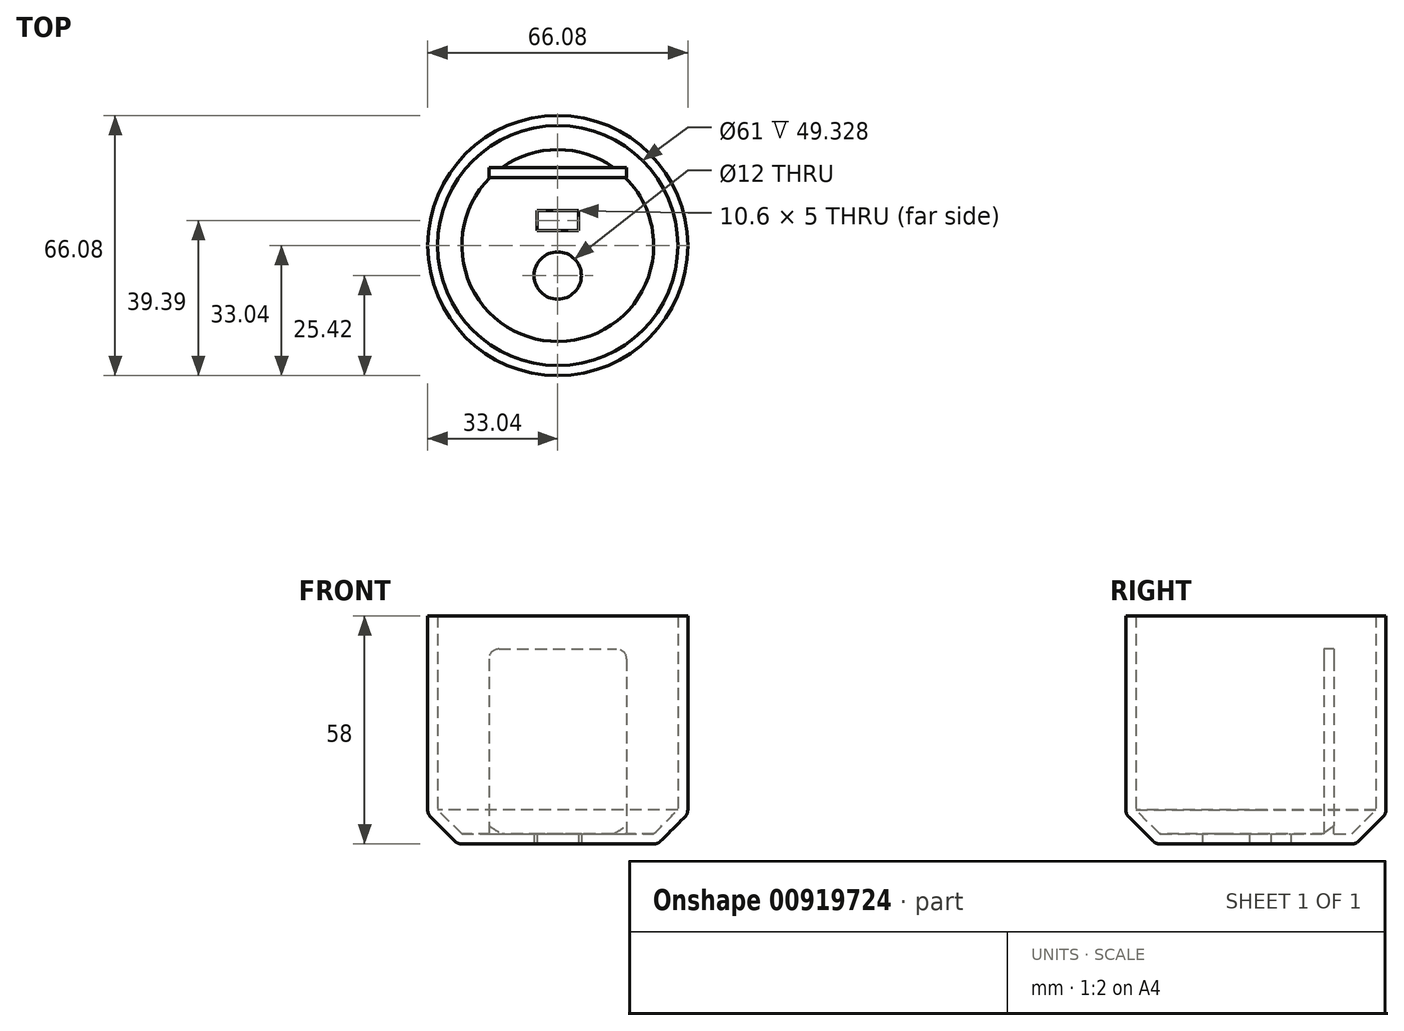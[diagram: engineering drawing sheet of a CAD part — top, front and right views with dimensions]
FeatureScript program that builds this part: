
annotation { "Feature Type Name" : "Feature", "Feature Type Description" : "" }
export const myFeature = defineFeature(function(context is Context, id is Id, definition is map)
    precondition{}
    {
        {
            var Q0;
            Q0=qCreatedBy(makeId("Top.planeOp"),FACE);
            var sketch = newSketch(context, id + "F0", { "sketchPlane" : qUnion([Q0])});
            skCircle(sketch, "E0", {"center": v(0, 0) * mm, "radius": 33.04 * mm});
            skSolve(sketch);
        }
        {
            var Q0;
            Q0 = qSketchRegion(id + "F0", true);
            extrude(context, id + "F1", {"entities" : qUnion([Q0]), "depth" : 58 * mm, "offsetDistance" : 25.4 * mm});
        }
        {
            var Q0;
            Q0=makeQuery(id+"F1.opExtrude","CAP_EDGE",EDGE,{"disambiguationData":[OSD([sQuery(id+"F0.wireOp",EDGE,"E0")])],"isStart":true});
            chamfer(context, id + "F2", {"entities" : qUnion([Q0]), "width" : 7.62 * mm, "tangentPropagation" : true});
        }
        {
            var Q0;
            Q0=makeQuery(id+"F1.opExtrude","CAP_FACE",FACE,{"disambiguationData":[OSD([sQuery(id+"F0.wireOp",EDGE,"E0")])],"isStart":false});
            shell(context, id + "F3", {"entities" : qUnion([Q0]), "thickness" : 2.54 * mm});
        }
        {
            var Q0;
            {var subQ0=sQuery(id+"F0.wireOp",EDGE,"E0");Q0=makeQuery(id+"F2.opChamfer","BLEND_EDGE",EDGE,{"blendedFrom":[makeQuery(id+"F1.opExtrude","CAP_EDGE",EDGE,{"disambiguationData":[OSD([subQ0])],"isStart":true}),makeQuery(id+"F1.opExtrude","SWEPT_FACE",FACE,{"disambiguationData":[OSD([subQ0])]})],"blendedInto":[makeQuery(id+"F1.opExtrude","SWEPT_FACE",FACE,{"disambiguationData":[OSD([subQ0])]})]});}
            var Q1;
            {var subQ0=sQuery(id+"F0.wireOp",EDGE,"E0");Q1=makeQuery(id+"F2.opChamfer","BLEND_EDGE",EDGE,{"blendedFrom":[makeQuery(id+"F1.opExtrude","CAP_EDGE",EDGE,{"disambiguationData":[OSD([subQ0])],"isStart":true}),makeQuery(id+"F1.opExtrude","CAP_FACE",FACE,{"disambiguationData":[OSD([subQ0])],"isStart":true})],"blendedInto":[makeQuery(id+"F1.opExtrude","CAP_FACE",FACE,{"disambiguationData":[OSD([subQ0])],"isStart":true})]});}
            fillet(context, id + "F4", {"entities" : qUnion([Q0, Q1]), "radius" : 2.54 * mm, "tangentPropagation" : true, "allowEdgeOverflow" : false});
        }
        {
            var Q0;
            Q0=makeQuery(id+"F1.opExtrude","CAP_FACE",FACE,{"disambiguationData":[OSD([sQuery(id+"F0.wireOp",EDGE,"E0")])],"isStart":true});
            var sketch = newSketch(context, id + "F5", { "sketchPlane" : qUnion([Q0])});
            skCircle(sketch, "E1", {"center": v(0, 7.62) * mm, "radius": 6 * mm});
            skLineSegment(sketch, "E2.bottom", {"start": v(-5.3, -3.85) * mm, "end": v(5.3, -3.85) * mm});
            skLineSegment(sketch, "E2.top", {"start": v(-5.3, -8.85) * mm, "end": v(5.3, -8.85) * mm});
            skLineSegment(sketch, "E2.left", {"start": v(-5.3, -3.85) * mm, "end": v(-5.3, -8.85) * mm});
            skLineSegment(sketch, "E2.right", {"start": v(5.3, -3.85) * mm, "end": v(5.3, -8.85) * mm});
            skPoint(sketch, "E2.middle", {"position": v(0, -6.35) * mm});
            skSolve(sketch);
        }
        {
            var Q0;
            Q0 = qSketchRegion(id + "F5", true);
            extrude(context, id + "F6", {"entities" : qUnion([Q0]), "operationType" : NewBodyOperationType.REMOVE, "endBound" : BoundingType.UP_TO_NEXT, "oppositeDirection" : true, "depth" : 25.4 * mm, "offsetDistance" : 25.4 * mm});
        }
        {
            var Q0;
            {var subQ0=sQuery(id+"F0.wireOp",EDGE,"E0");Q0=makeQuery(id+"F3.opShell","OFFSET_FACE",FACE,{"disambiguationData":[OSD([subQ0]),TDD([makeQuery(id+"F1.opExtrude","CAP_FACE",FACE,{"disambiguationData":[OSD([subQ0])],"isStart":true})])]});}
            var sketch = newSketch(context, id + "F7", { "sketchPlane" : qUnion([Q0])});
            skLineSegment(sketch, "E3.bottom", {"start": v(-17.5, 19.85) * mm, "end": v(17.5, 19.85) * mm});
            skLineSegment(sketch, "E3.top", {"start": v(-17.5, 17.31) * mm, "end": v(17.5, 17.31) * mm});
            skLineSegment(sketch, "E3.left", {"start": v(-17.5, 19.85) * mm, "end": v(-17.5, 17.31) * mm});
            skLineSegment(sketch, "E3.right", {"start": v(17.5, 19.85) * mm, "end": v(17.5, 17.31) * mm});
            skPoint(sketch, "E3.middle", {"position": v(0, 18.58) * mm});
            skSolve(sketch);
        }
        {
            var Q0;
            Q0 = qSketchRegion(id + "F7", true);
            extrude(context, id + "F8", {"entities" : qUnion([Q0]), "operationType" : NewBodyOperationType.ADD, "depth" : 47 * mm, "offsetDistance" : 25.4 * mm});
        }
        {
            var Q0;
            Q0=makeQuery(id+"F8.opExtrude","CAP_EDGE",EDGE,{"disambiguationData":[OSD([sQuery(id+"F7.wireOp",EDGE,"E3.left")])],"isStart":false});
            var Q1;
            Q1=makeQuery(id+"F8.opExtrude","CAP_EDGE",EDGE,{"disambiguationData":[OSD([sQuery(id+"F7.wireOp",EDGE,"E3.right")])],"isStart":false});
            fillet(context, id + "F9", {"entities" : qUnion([Q0, Q1]), "radius" : 2.54 * mm, "tangentPropagation" : true, "allowEdgeOverflow" : false});
        }
    });
